# Revit family: Profim Xenon
name_source: partatom
category: Furniture
revit_build: Autodesk Revit Architecture 2015 (Build: 20140322_1515(x64)
units: mm (PartAtom-declared; Revit-internal decimal feet)

## types (1)
- Profim Xenon 11STL
    Armrest material = ProfiM - Xenon - Armrest
    Backrest Frame material = ProfiM - Xenon - Backrest frame
    Backrest Support Material = ProfiM - Xenon - Backrest support
    Backrest material = ProfiM - Xenon - Backrest
    Base material = ProfiM - Xenon - Base
    Damper Lower material = ProfiM - Xenon - Damper lower
    Damper Upper material = ProfiM - Xenon - Damper upper
    Description = swivel armchair, high backrest, 5-star base on wheels
    Headrest Frame material = ProfiM - Xenon - Headrest Frame
    Headrest material = ProfiM - Xenon - Headrest
    Manufacturer = Profim
    Model = Xenon 11STL
    Seat Material = ProfiM - Xenon - Seat
    Seat Mechanism Material = ProfiM - Xenon - Mechanism
    Seat Support material = ProfiM - Xenon - Seat Support
    Wheels material = ProfiM - Xenon - Wheels

## geometry (parser evidence)
native form markers: Sweep x2
no freeform markers — native parametric forms only
